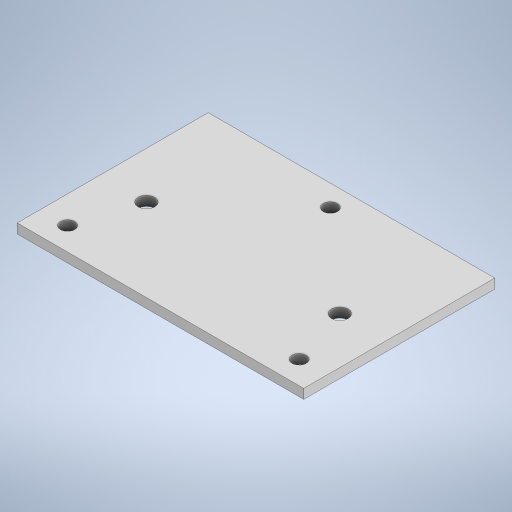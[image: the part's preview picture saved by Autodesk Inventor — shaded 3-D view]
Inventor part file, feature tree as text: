
AUTODESK INVENTOR PART (.ipt)
format: ipt  version: 2023 (Build 270158000, 158)  size: 216,064 bytes
history: native  units: mm
features: other x1, extrude x1, sketch x1
ambient origin geometry x8: Origin, YZ Plane, XZ Plane, XY Plane, X Axis, Y Axis, Z Axis, Center Point
bodies: Body1 (feature_tree)
feature tree (3):
  other  "Bryła1"
  extrude  "Wyciągnięcie proste1"  Depth=40.0mm
  sketch  "Szkic1"
